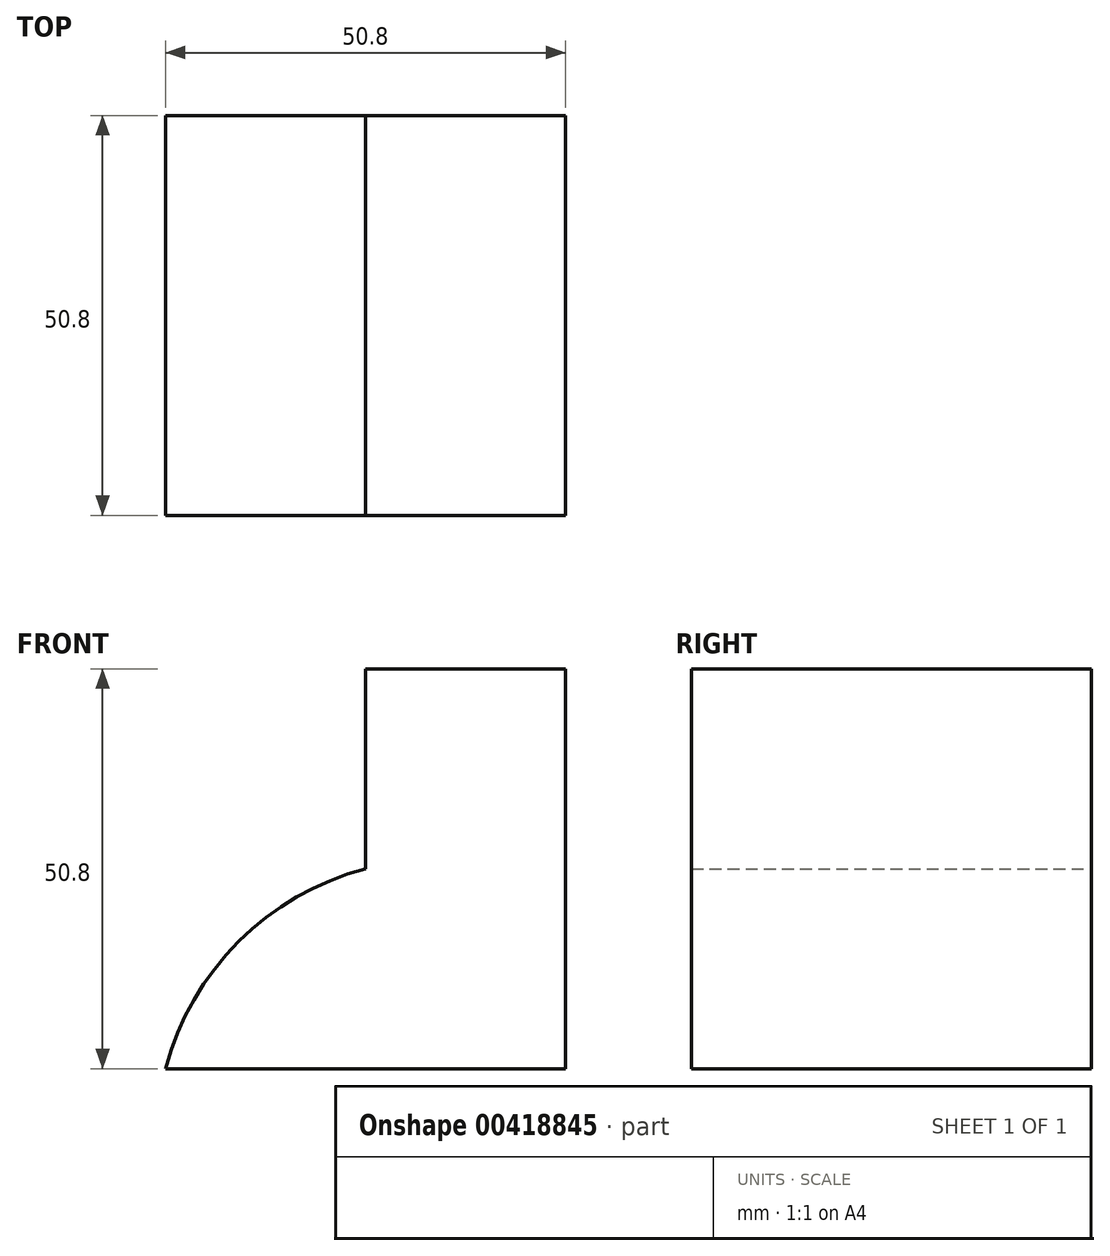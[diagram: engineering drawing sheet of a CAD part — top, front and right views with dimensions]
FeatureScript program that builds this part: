
annotation { "Feature Type Name" : "Feature", "Feature Type Description" : "" }
export const myFeature = defineFeature(function(context is Context, id is Id, definition is map)
    precondition{}
    {
        {
            var Q0;
            Q0=qCreatedBy(makeId("Front.planeOp"),FACE);
            var sketch = newSketch(context, id + "F0", { "sketchPlane" : qUnion([Q0])});
            skLineSegment(sketch, "E0", {"start": v(0, 0) * mm, "end": v(-50.8, 0) * mm});
            skLineSegment(sketch, "E1", {"start": v(0, 0) * mm, "end": v(0, 50.8) * mm});
            skLineSegment(sketch, "E2", {"start": v(0, 50.8) * mm, "end": v(-25.4, 50.8) * mm});
            skLineSegment(sketch, "E3", {"start": v(-25.4, 50.8) * mm, "end": v(-25.4, 25.4) * mm});
            skArc(sketch, "E4", {"start": v(-25.4, 25.4) * mm, "mid": v(-41.54, 16.14) * mm, "end": v(-50.8, 0) * mm});
            skSolve(sketch);
        }
        {
            var Q0;
            Q0 = qSketchRegion(id + "F0", true);
            extrude(context, id + "F1", {"entities" : qUnion([Q0]), "depth" : 50.8 * mm});
        }
    });
